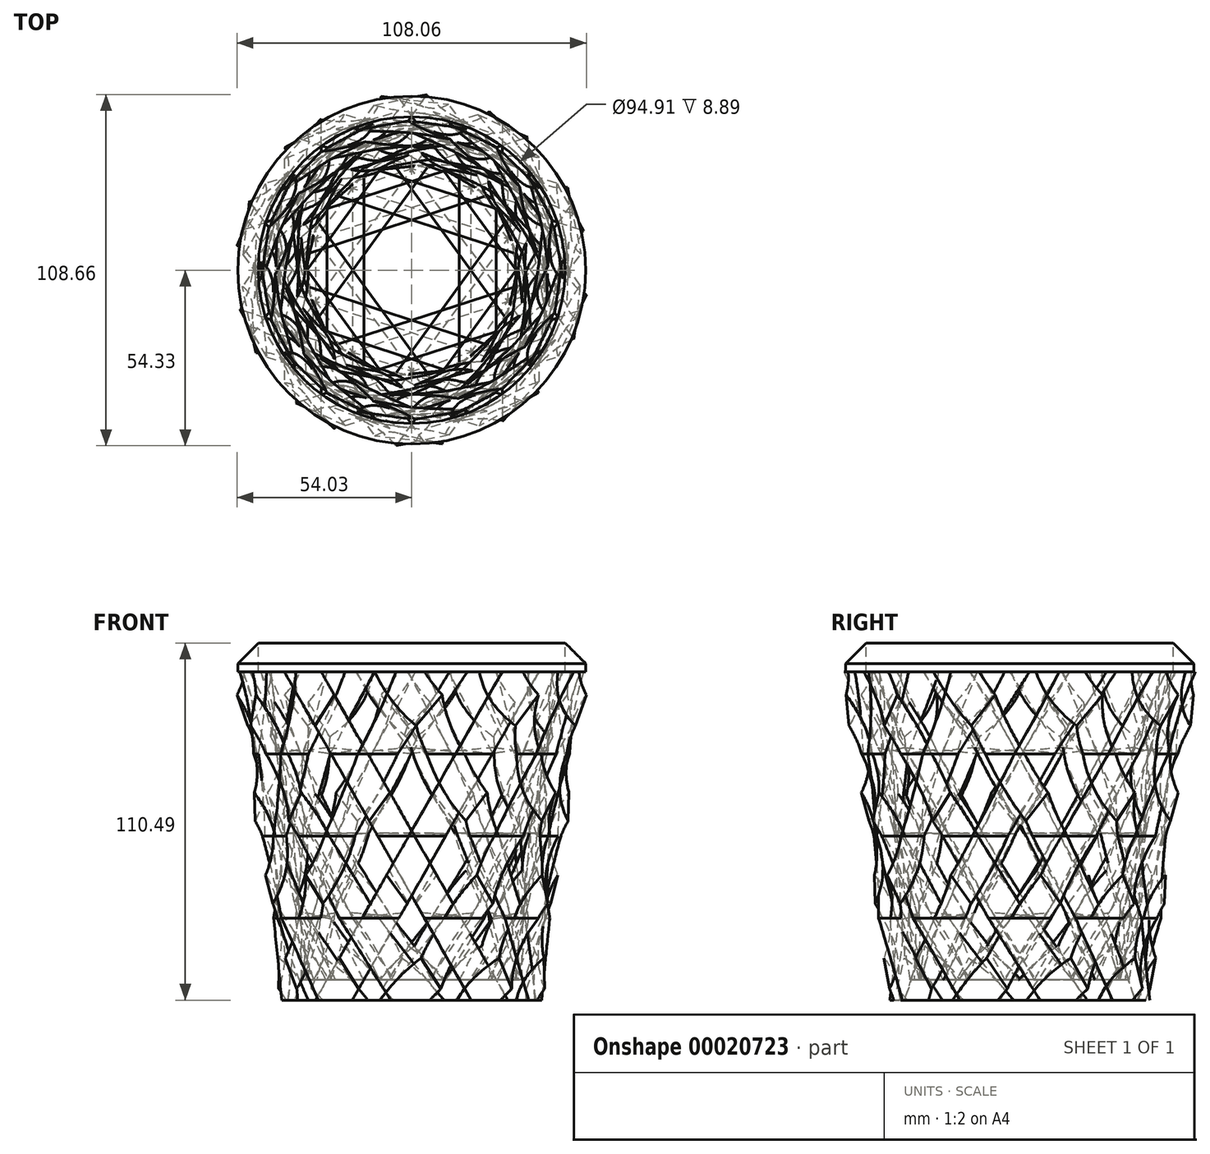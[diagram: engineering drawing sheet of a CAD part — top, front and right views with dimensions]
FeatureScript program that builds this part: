
annotation { "Feature Type Name" : "Feature", "Feature Type Description" : "" }
export const myFeature = defineFeature(function(context is Context, id is Id, definition is map)
    precondition{}
    {
        {
            var Q0;
            Q0=qCreatedBy(makeId("Top.planeOp"),FACE);
            var sketch = newSketch(context, id + "F0", { "sketchPlane" : qUnion([Q0])});
            skCircle(sketch, "E0.cCircle", {"center": v(0, 0) * mm, "radius": 38.1 * mm, "construction": true});
            skLineSegment(sketch, "E0.0", {"start": v(38.73, -14.17) * mm, "end": v(17.37, -37.4) * mm});
            skLineSegment(sketch, "E0.1", {"start": v(17.37, -37.4) * mm, "end": v(-14.17, -38.73) * mm});
            skLineSegment(sketch, "E0.2", {"start": v(-14.17, -38.73) * mm, "end": v(-37.4, -17.37) * mm});
            skLineSegment(sketch, "E0.3", {"start": v(-37.4, -17.37) * mm, "end": v(-38.73, 14.17) * mm});
            skLineSegment(sketch, "E0.4", {"start": v(-38.73, 14.17) * mm, "end": v(-17.37, 37.4) * mm});
            skLineSegment(sketch, "E0.5", {"start": v(-17.37, 37.4) * mm, "end": v(14.17, 38.73) * mm});
            skLineSegment(sketch, "E0.6", {"start": v(14.17, 38.73) * mm, "end": v(37.4, 17.37) * mm});
            skLineSegment(sketch, "E0.7", {"start": v(37.4, 17.37) * mm, "end": v(38.73, -14.17) * mm});
            skPoint(sketch, "E0.0.midPoint", {"position": v(28.05, -25.78) * mm});
            skSolve(sketch);
        }
        {
            var Q0;
            Q0=makeQuery(id+"F0.imprint","IMPRINT",FACE,{"disambiguationData":[TD([[makeQuery(id+"F0.imprint","IMPRINT",EDGE,{"derivedFrom":sQuery(id+"F0.wireOp",EDGE,"E0.0")}),-1.0]])]});
            cPlane(context, id + "F1", {"entities" : qUnion([Q0]), "cplaneType" : CPlaneType.OFFSET, "offset" : 25.4 * mm, "width" : 152.4 * mm, "height" : 152.4 * mm});
        }
        {
            var Q0;
            Q0=qCreatedBy(id+"F1.planeOp",FACE);
            var sketch = newSketch(context, id + "F2", { "sketchPlane" : qUnion([Q0])});
            skPoint(sketch, "E1.0", {"position": v(-14.17, -38.73) * mm});
            skCircle(sketch, "E2.cCircle", {"center": v(0, 0) * mm, "radius": 41.24 * mm, "construction": true});
            skLineSegment(sketch, "E2.0", {"start": v(1.88, -44.6) * mm, "end": v(-30.2, -32.86) * mm});
            skLineSegment(sketch, "E2.1", {"start": v(-30.2, -32.86) * mm, "end": v(-44.6, -1.88) * mm});
            skLineSegment(sketch, "E2.2", {"start": v(-44.6, -1.88) * mm, "end": v(-32.86, 30.2) * mm});
            skLineSegment(sketch, "E2.3", {"start": v(-32.86, 30.2) * mm, "end": v(-1.88, 44.6) * mm});
            skLineSegment(sketch, "E2.4", {"start": v(-1.88, 44.6) * mm, "end": v(30.2, 32.86) * mm});
            skLineSegment(sketch, "E2.5", {"start": v(30.2, 32.86) * mm, "end": v(44.6, 1.88) * mm});
            skLineSegment(sketch, "E2.6", {"start": v(44.6, 1.88) * mm, "end": v(32.86, -30.2) * mm});
            skLineSegment(sketch, "E2.7", {"start": v(32.86, -30.2) * mm, "end": v(1.88, -44.6) * mm});
            skSolve(sketch);
        }
        {
            var Q0;
            Q0=makeQuery(id+"F0.imprint","IMPRINT",FACE,{"disambiguationData":[TD([[makeQuery(id+"F0.imprint","IMPRINT",EDGE,{"derivedFrom":sQuery(id+"F0.wireOp",EDGE,"E0.0")}),-1.0]])]});
            var Q1;
            Q1=makeQuery(id+"F2.imprint","IMPRINT",FACE,{"disambiguationData":[TD([[makeQuery(id+"F2.imprint","IMPRINT",EDGE,{"derivedFrom":sQuery(id+"F2.wireOp",EDGE,"E2.0")}),-1.0]])]});
            loft(context, id + "F3", {"sheetProfilesArray" : [{ "sheetProfileEntities" : qUnion([Q0]) }, { "sheetProfileEntities" : qUnion([Q1]) }]});
        }
        {
            var Q0;
            Q0=makeQuery(id+"F3.opLoft","CAP_FACE",FACE,{"disambiguationData":[OSD([makeQuery(id+"F2.imprint","IMPRINT",FACE,{"disambiguationData":[TD([[makeQuery(id+"F2.imprint","IMPRINT",EDGE,{"derivedFrom":sQuery(id+"F2.wireOp",EDGE,"E2.0")}),-1.0]])]})])],"isStart":true});
            cPlane(context, id + "F4", {"entities" : qUnion([Q0]), "cplaneType" : CPlaneType.OFFSET, "offset" : 25.4 * mm, "width" : 152.4 * mm, "height" : 152.4 * mm});
        }
        {
            var Q0;
            Q0=qCreatedBy(id+"F4.planeOp",FACE);
            var sketch = newSketch(context, id + "F5", { "sketchPlane" : qUnion([Q0])});
            skPoint(sketch, "E3.0", {"position": v(1.88, -44.6) * mm});
            skCircle(sketch, "E4.cCircle", {"center": v(0, 0) * mm, "radius": 44.64 * mm, "construction": true});
            skLineSegment(sketch, "E4.0", {"start": v(20.35, -43.82) * mm, "end": v(-16.6, -45.37) * mm});
            skLineSegment(sketch, "E4.1", {"start": v(-16.6, -45.37) * mm, "end": v(-43.82, -20.35) * mm});
            skLineSegment(sketch, "E4.2", {"start": v(-43.82, -20.35) * mm, "end": v(-45.37, 16.6) * mm});
            skLineSegment(sketch, "E4.3", {"start": v(-45.37, 16.6) * mm, "end": v(-20.35, 43.82) * mm});
            skLineSegment(sketch, "E4.4", {"start": v(-20.35, 43.82) * mm, "end": v(16.6, 45.37) * mm});
            skLineSegment(sketch, "E4.5", {"start": v(16.6, 45.37) * mm, "end": v(43.82, 20.35) * mm});
            skLineSegment(sketch, "E4.6", {"start": v(43.82, 20.35) * mm, "end": v(45.37, -16.6) * mm});
            skLineSegment(sketch, "E4.7", {"start": v(45.37, -16.6) * mm, "end": v(20.35, -43.82) * mm});
            skSolve(sketch);
        }
        {
            var Q1;
            Q1=makeQuery(id+"F3.opLoft","CAP_FACE",FACE,{"disambiguationData":[OSD([makeQuery(id+"F2.imprint","IMPRINT",FACE,{"disambiguationData":[TD([[makeQuery(id+"F2.imprint","IMPRINT",EDGE,{"derivedFrom":sQuery(id+"F2.wireOp",EDGE,"E2.0")}),-1.0]])]})])],"isStart":true});
            var Q2;
            Q2=makeQuery(id+"F5.imprint","IMPRINT",FACE,{"disambiguationData":[TD([[makeQuery(id+"F5.imprint","IMPRINT",EDGE,{"derivedFrom":sQuery(id+"F5.wireOp",EDGE,"E4.0")}),-1.0]])]});
            loft(context, id + "F6", {"operationType" : NewBodyOperationType.ADD, "sheetProfilesArray" : [{ "sheetProfileEntities" : qUnion([Q1]) }, { "sheetProfileEntities" : qUnion([Q2]) }]});
        }
        {
            var Q0;
            Q0=qCreatedBy(id+"F4.planeOp",FACE);
            cPlane(context, id + "F7", {"entities" : qUnion([Q0]), "cplaneType" : CPlaneType.OFFSET, "offset" : 25.4 * mm, "width" : 152.4 * mm, "height" : 152.4 * mm});
        }
        {
            var Q0;
            Q0=qCreatedBy(id+"F7.planeOp",FACE);
            var sketch = newSketch(context, id + "F8", { "sketchPlane" : qUnion([Q0])});
            skPoint(sketch, "E5.0", {"position": v(16.6, 45.37) * mm});
            skCircle(sketch, "E6.cCircle", {"center": v(0, 0) * mm, "radius": 48.31 * mm, "construction": true});
            skLineSegment(sketch, "E6.0", {"start": v(-2.2, 52.25) * mm, "end": v(35.4, 38.5) * mm});
            skLineSegment(sketch, "E6.1", {"start": v(35.4, 38.5) * mm, "end": v(52.25, 2.2) * mm});
            skLineSegment(sketch, "E6.2", {"start": v(52.25, 2.2) * mm, "end": v(38.5, -35.4) * mm});
            skLineSegment(sketch, "E6.3", {"start": v(38.5, -35.4) * mm, "end": v(2.2, -52.25) * mm});
            skLineSegment(sketch, "E6.4", {"start": v(2.2, -52.25) * mm, "end": v(-35.4, -38.5) * mm});
            skLineSegment(sketch, "E6.5", {"start": v(-35.4, -38.5) * mm, "end": v(-52.25, -2.2) * mm});
            skLineSegment(sketch, "E6.6", {"start": v(-52.25, -2.2) * mm, "end": v(-38.5, 35.4) * mm});
            skLineSegment(sketch, "E6.7", {"start": v(-38.5, 35.4) * mm, "end": v(-2.2, 52.25) * mm});
            skSolve(sketch);
        }
        {
            var Q1;
            Q1=makeQuery(id+"F6.opLoft","CAP_FACE",FACE,{"disambiguationData":[OSD([makeQuery(id+"F5.imprint","IMPRINT",FACE,{"disambiguationData":[TD([[makeQuery(id+"F5.imprint","IMPRINT",EDGE,{"derivedFrom":sQuery(id+"F5.wireOp",EDGE,"E4.0")}),-1.0]])]})])],"isStart":true});
            var Q2;
            Q2=makeQuery(id+"F8.imprint","IMPRINT",FACE,{"disambiguationData":[TD([[makeQuery(id+"F8.imprint","IMPRINT",EDGE,{"derivedFrom":sQuery(id+"F8.wireOp",EDGE,"E6.0")}),-1.0]])]});
            loft(context, id + "F9", {"operationType" : NewBodyOperationType.ADD, "sheetProfilesArray" : [{ "sheetProfileEntities" : qUnion([Q1]) }, { "sheetProfileEntities" : qUnion([Q2]) }]});
        }
        {
            var Q0;
            Q0=qCreatedBy(id+"F7.planeOp",FACE);
            cPlane(context, id + "F10", {"entities" : qUnion([Q0]), "cplaneType" : CPlaneType.OFFSET, "offset" : 25.4 * mm, "width" : 152.4 * mm, "height" : 152.4 * mm});
        }
        {
            var Q0;
            Q0=qCreatedBy(id+"F10.planeOp",FACE);
            var sketch = newSketch(context, id + "F11", { "sketchPlane" : qUnion([Q0])});
            skPoint(sketch, "E7.0", {"position": v(35.4, 38.5) * mm});
            skCircle(sketch, "E8.cCircle", {"center": v(0, 0) * mm, "radius": 52.3 * mm, "construction": true});
            skLineSegment(sketch, "E8.0", {"start": v(19.44, 53.16) * mm, "end": v(51.34, 23.84) * mm});
            skLineSegment(sketch, "E8.1", {"start": v(51.34, 23.84) * mm, "end": v(53.16, -19.44) * mm});
            skLineSegment(sketch, "E8.2", {"start": v(53.16, -19.44) * mm, "end": v(23.84, -51.34) * mm});
            skLineSegment(sketch, "E8.3", {"start": v(23.84, -51.34) * mm, "end": v(-19.44, -53.16) * mm});
            skLineSegment(sketch, "E8.4", {"start": v(-19.44, -53.16) * mm, "end": v(-51.34, -23.84) * mm});
            skLineSegment(sketch, "E8.5", {"start": v(-51.34, -23.84) * mm, "end": v(-53.16, 19.44) * mm});
            skLineSegment(sketch, "E8.6", {"start": v(-53.16, 19.44) * mm, "end": v(-23.84, 51.34) * mm});
            skLineSegment(sketch, "E8.7", {"start": v(-23.84, 51.34) * mm, "end": v(19.44, 53.16) * mm});
            skSolve(sketch);
        }
        {
            var Q1;
            Q1=makeQuery(id+"F9.opLoft","CAP_FACE",FACE,{"disambiguationData":[OSD([makeQuery(id+"F8.imprint","IMPRINT",FACE,{"disambiguationData":[TD([[makeQuery(id+"F8.imprint","IMPRINT",EDGE,{"derivedFrom":sQuery(id+"F8.wireOp",EDGE,"E6.0")}),-1.0]])]})])],"isStart":true});
            var Q2;
            Q2=makeQuery(id+"F11.imprint","IMPRINT",FACE,{"disambiguationData":[TD([[makeQuery(id+"F11.imprint","IMPRINT",EDGE,{"derivedFrom":sQuery(id+"F11.wireOp",EDGE,"E8.0")}),-1.0]])]});
            loft(context, id + "F12", {"operationType" : NewBodyOperationType.ADD, "sheetProfilesArray" : [{ "sheetProfileEntities" : qUnion([Q1]) }, { "sheetProfileEntities" : qUnion([Q2]) }]});
        }
        {
            var Q0;
            Q0=makeQuery(id+"F12.opLoft","CAP_FACE",FACE,{"disambiguationData":[OSD([makeQuery(id+"F11.imprint","IMPRINT",FACE,{"disambiguationData":[TD([[makeQuery(id+"F11.imprint","IMPRINT",EDGE,{"derivedFrom":sQuery(id+"F11.wireOp",EDGE,"E8.0")}),-1.0]])]})])],"isStart":true});
            shell(context, id + "F13", {"entities" : qUnion([Q0]), "thickness" : 6.35 * mm});
        }
        {
            var Q0;
            Q0=qCreatedBy(makeId("Front.planeOp"),FACE);
            var sketch = newSketch(context, id + "F14", { "sketchPlane" : qUnion([Q0])});
            skLineSegment(sketch, "E9", {"start": v(-41.72, 125.7) * mm, "end": v(29.76, 0) * mm});
            skLineSegment(sketch, "E10", {"start": v(29.76, 0) * mm, "end": v(18.36, 0) * mm});
            skLineSegment(sketch, "E11", {"start": v(18.36, 0) * mm, "end": v(-54.17, 127.55) * mm});
            skLineSegment(sketch, "E12", {"start": v(-54.17, 127.55) * mm, "end": v(-41.72, 125.7) * mm});
            skLineSegment(sketch, "E13", {"start": v(0, 0) * mm, "end": v(0, 150.78) * mm, "construction": true});
            skSolve(sketch);
        }
        {
            var Q0;
            Q0=makeQuery(id+"F14.imprint","IMPRINT",FACE,{"disambiguationData":[TD([[makeQuery(id+"F14.imprint","IMPRINT",EDGE,{"derivedFrom":sQuery(id+"F14.wireOp",EDGE,"E9")}),-1.0]])]});
            extrude(context, id + "F15", {"entities" : qUnion([Q0]), "endBound" : BoundingType.SYMMETRIC, "depth" : 254 * mm});
        }
        {
            var Q0;
            Q0=makeQuery(id+"F3.opLoft","SWEPT_BODY",BODY,{"disambiguationData":[OSD([makeQuery(id+"F0.imprint","IMPRINT",FACE,{"disambiguationData":[TD([[makeQuery(id+"F0.imprint","IMPRINT",EDGE,{"derivedFrom":sQuery(id+"F0.wireOp",EDGE,"E0.0")}),-1.0]])]}),makeQuery(id+"F2.imprint","IMPRINT",FACE,{"disambiguationData":[TD([[makeQuery(id+"F2.imprint","IMPRINT",EDGE,{"derivedFrom":sQuery(id+"F2.wireOp",EDGE,"E2.0")}),-1.0]])]})])]});
            var Q1;
            Q1=makeQuery(id+"F15.opExtrude","SWEPT_BODY",BODY,{"disambiguationData":[OSD([sQuery(id+"F14.wireOp",EDGE,"E9"),sQuery(id+"F14.wireOp",EDGE,"E10"),sQuery(id+"F14.wireOp",EDGE,"E11"),sQuery(id+"F14.wireOp",EDGE,"E12")])]});
            booleanBodies(context, id + "F16", {"operationType" : BooleanOperationType.INTERSECTION, "tools" : qUnion([Q0, Q1])});
        }
        {
            var Q0;
            Q0=makeQuery(id+"F16.opBoolean","INTERSECT",BODY,{"derivedFrom":[makeQuery(id+"F3.opLoft","SWEPT_BODY",BODY,{"disambiguationData":[OSD([makeQuery(id+"F0.imprint","IMPRINT",FACE,{"disambiguationData":[TD([[makeQuery(id+"F0.imprint","IMPRINT",EDGE,{"derivedFrom":sQuery(id+"F0.wireOp",EDGE,"E0.0")}),-1.0]])]}),makeQuery(id+"F2.imprint","IMPRINT",FACE,{"disambiguationData":[TD([[makeQuery(id+"F2.imprint","IMPRINT",EDGE,{"derivedFrom":sQuery(id+"F2.wireOp",EDGE,"E2.0")}),-1.0]])]})])]}),makeQuery(id+"F15.opExtrude","SWEPT_BODY",BODY,{"disambiguationData":[OSD([sQuery(id+"F14.wireOp",EDGE,"E9"),sQuery(id+"F14.wireOp",EDGE,"E10"),sQuery(id+"F14.wireOp",EDGE,"E11"),sQuery(id+"F14.wireOp",EDGE,"E12")])]})]});
            var Q1;
            Q1=sQuery(id+"F14.wireOp",EDGE,"E13");
            circularPattern(context, id + "F17", {"entities" : qUnion([Q0]), "axis" : qUnion([Q1]), "angle" : 360 * degree, "instanceCount" : 10, "equalSpace" : true});
        }
        {
            var Q0;
            {var subQ0=sQuery(id+"F11.wireOp",EDGE,"E8.5");var subQ1=sQuery(id+"F11.wireOp",EDGE,"E8.4");var subQ2=sQuery(id+"F11.wireOp",EDGE,"E8.3");var subQ3=sQuery(id+"F8.wireOp",EDGE,"E6.6");var subQ4=sQuery(id+"F8.wireOp",EDGE,"E6.5");var subQ5=sQuery(id+"F8.wireOp",EDGE,"E6.4");Q0=makeQuery(id+"F17.opPattern","COPY",FACE,{"derivedFrom":makeQuery(id+"F16.opBoolean","SPLIT",FACE,{"disambiguationData":[TD([makeQuery(id+"F12.opLoft","SWEPT_FACE",FACE,{"disambiguationData":[OSD([subQ5,subQ4,subQ3,subQ2,subQ1,subQ0])]})])],"derivedFrom":makeQuery(id+"F12.opLoft","CAP_FACE",FACE,{"disambiguationData":[OSD([makeQuery(id+"F11.imprint","IMPRINT",FACE,{"disambiguationData":[TD([[makeQuery(id+"F11.imprint","IMPRINT",EDGE,{"derivedFrom":sQuery(id+"F11.wireOp",EDGE,"E8.0")}),-1.0]])]})])],"isStart":true})}),"instanceName":"7"});}
            var sketch = newSketch(context, id + "F18", { "sketchPlane" : qUnion([Q0])});
            skCircle(sketch, "E14", {"center": v(0, 0) * mm, "radius": 53.8 * mm});
            skCircle(sketch, "E15.0", {"center": v(0, 0) * mm, "radius": 47.46 * mm});
            skSolve(sketch);
        }
        {
            var Q0;
            Q0=makeQuery(id+"F18.imprint","IMPRINT",FACE,{"disambiguationData":[TD([[makeQuery(id+"F18.imprint","IMPRINT",EDGE,{"derivedFrom":sQuery(id+"F18.wireOp",EDGE,"E14")}),1.0]])]});
            cPlane(context, id + "F19", {"entities" : qUnion([Q0]), "cplaneType" : CPlaneType.OFFSET, "offset" : 12.7 * mm, "width" : 152.4 * mm, "height" : 152.4 * mm});
        }
        {
            var Q0;
            Q0=qCreatedBy(id+"F19.planeOp",FACE);
            var sketch = newSketch(context, id + "F20", { "sketchPlane" : qUnion([Q0])});
            skCircle(sketch, "E16.0", {"center": v(0, 0) * mm, "radius": 53.8 * mm});
            skCircle(sketch, "E17.0", {"center": v(0, 0) * mm, "radius": 47.46 * mm});
            skSolve(sketch);
        }
        {
            var Q0;
            Q0=makeQuery(id+"F20.imprint","IMPRINT",FACE,{"disambiguationData":[TD([[makeQuery(id+"F20.imprint","IMPRINT",EDGE,{"derivedFrom":sQuery(id+"F20.wireOp",EDGE,"E16.0")}),1.0]])]});
            extrude(context, id + "F21", {"entities" : qUnion([Q0]), "oppositeDirection" : true, "depth" : 12.7 * mm});
        }
        {
            var Q0;
            Q0=makeQuery(id+"F21.opExtrude","CAP_EDGE",EDGE,{"disambiguationData":[OSD([sQuery(id+"F20.wireOp",EDGE,"E16.0")])],"isStart":true});
            chamfer(context, id + "F22", {"entities" : qUnion([Q0]), "width" : 10.16 * mm, "tangentPropagation" : true});
        }
    });
